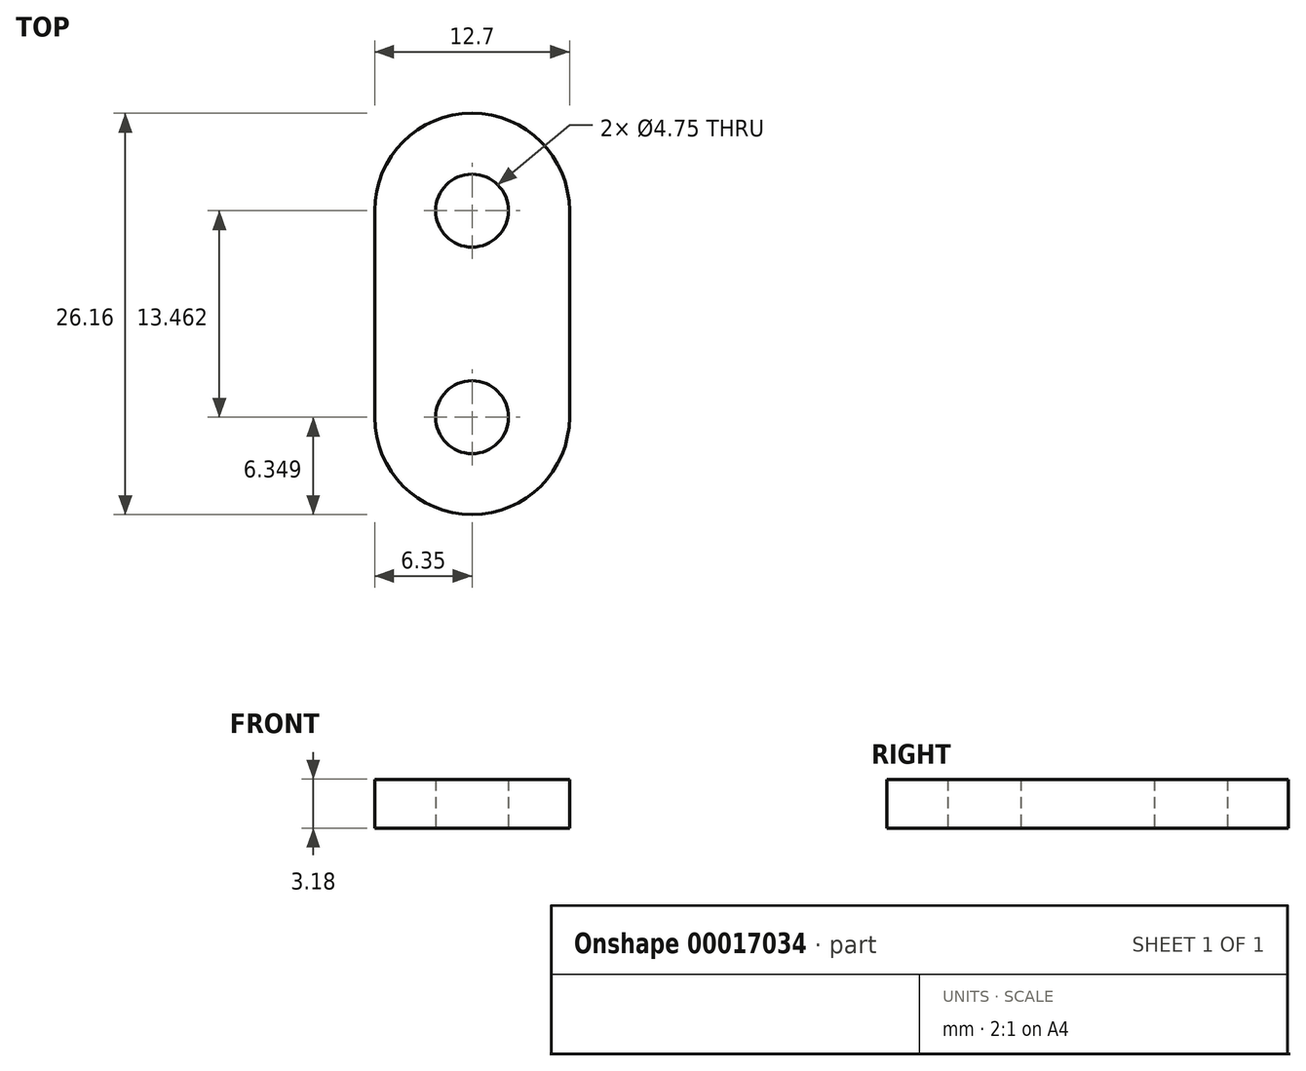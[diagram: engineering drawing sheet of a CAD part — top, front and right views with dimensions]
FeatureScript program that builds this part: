
annotation { "Feature Type Name" : "Feature", "Feature Type Description" : "" }
export const myFeature = defineFeature(function(context is Context, id is Id, definition is map)
    precondition{}
    {
        {
            var Q0;
            Q0=qCreatedBy(makeId("Top.planeOp"),FACE);
            var sketch = newSketch(context, id + "F0", { "sketchPlane" : qUnion([Q0])});
            skLineSegment(sketch, "E0.rect.bottom", {"start": v(0, 13.08) * mm, "end": v(0, 13.08) * mm});
            skLineSegment(sketch, "E0.rect.top", {"start": v(0, -13.08) * mm, "end": v(0, -13.08) * mm});
            skLineSegment(sketch, "E0.rect.left", {"start": v(6.35, 6.73) * mm, "end": v(6.35, -6.73) * mm});
            skLineSegment(sketch, "E0.rect.right", {"start": v(-6.35, 6.73) * mm, "end": v(-6.35, -6.73) * mm});
            skPoint(sketch, "E0.rect.middle", {"position": v(0, 0) * mm});
            skCircle(sketch, "E1", {"center": v(0, 6.73) * mm, "radius": 2.37 * mm});
            skCircle(sketch, "E2", {"center": v(0, -6.73) * mm, "radius": 2.37 * mm});
            skArc(sketch, "E3.filletArc", {"start": v(0, 13.08) * mm, "mid": v(-4.5, 11.22) * mm, "end": v(-6.35, 6.73) * mm});
            skArc(sketch, "E4.filletArc", {"start": v(6.35, 6.73) * mm, "mid": v(4.5, 11.22) * mm, "end": v(0, 13.08) * mm});
            skArc(sketch, "E5.filletArc", {"start": v(0, -13.08) * mm, "mid": v(4.5, -11.22) * mm, "end": v(6.35, -6.73) * mm});
            skArc(sketch, "E6.filletArc", {"start": v(-6.35, -6.73) * mm, "mid": v(-4.5, -11.22) * mm, "end": v(0, -13.08) * mm});
            skSolve(sketch);
        }
        {
            var Q0;
            Q0 = qSketchRegion(id + "F0", true);
            extrude(context, id + "F1", {"entities" : qUnion([Q0]), "depth" : 3.17 * mm});
        }
    });
